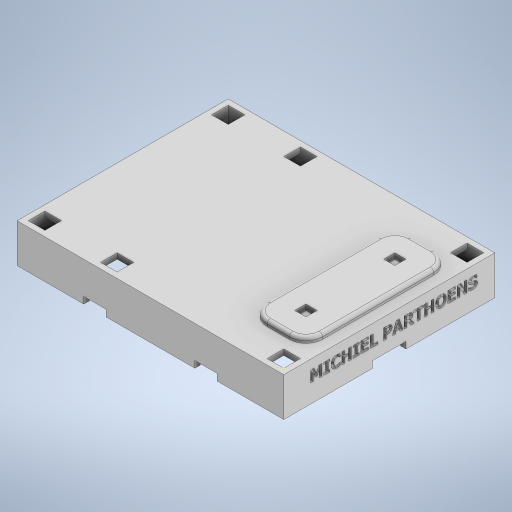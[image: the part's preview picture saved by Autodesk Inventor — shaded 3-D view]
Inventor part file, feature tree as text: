
AUTODESK INVENTOR PART (.ipt)
format: ipt  version: 2023 (Build 270158000, 158)  size: 671,232 bytes
history: native  units: mm
features: extrude x8, sketch x8, fillet x2
ambient origin geometry x8: Origin, YZ Plane, XZ Plane, XY Plane, X Axis, Y Axis, Z Axis, Center Point
bodies: Solid1 (feature_tree)
feature tree (18):
  extrude  "Extrusion1"  Depth=230.0mm
  extrude  "Extrusion2"  Depth=5.0mm
  extrude  "Extrusion3"  Depth=5.0mm
  extrude  "Extrusion4"  Depth=75.0mm
  fillet  "Fillet1"  Radius=75.0mm
  fillet  "Fillet2"  Radius=20.0mm
  extrude  "Extrusion5"  Depth=20.0mm
  extrude  "Extrusion6"  Depth=55.0mm
  extrude  "Extrusion7"  Depth=20.0mm
  sketch  "Sketch8"  dims[d16=55.0mm d17=20.0mm]
  extrude  "Extrusion8"  Depth=2.5mm TaperAngle=0.0deg
  sketch  "Sketch1"  dims[d0=180.0mm d1=230.0mm]
  sketch  "Sketch2"  dims[d2=5.0mm d3=5.0mm]
  sketch  "Sketch3"  dims[d4=5.0mm d5=5.0mm]
  sketch  "Sketch4"  dims[d6=30.0mm d7=75.0mm d8=75.0mm d9=20.0mm]
  sketch  "Sketch5"  dims[d10=20.0mm d12=20.0mm]
  sketch  "Sketch7"  dims[d14=80.0mm d15=55.0mm]
  sketch  "Sketch9"  dims[d18=80.0mm d19=6.0mm d20=0.0mm d21=24.0mm d22=0.0mm d23=5.0mm d24=0.0mm d25=130.0mm d26=30.0mm d27=30.0mm d28=10.0mm d29=50.0mm d30=5.0mm d31=0.0mm d32=15.0mm d33=3.0mm d34=10.0mm d35=10.0mm d36=20.0mm d37=20.0mm d40=10.0mm d41=10.0mm d42=20.0mm d43=20.0mm d44=5.0mm d45=0.0mm d46=15.0mm d47=15.0mm d51=15.0mm d52=15.0mm d53=15.0mm d54=15.0mm d55=15.0mm d56=15.0mm d57=15.0mm d58=15.0mm d59=50.0mm d60=5.0mm d61=0.0mm d62=5.0mm d63=0.0mm d64=15.0mm d65=15.0mm d66=2.5mm d67=0.0mm]
